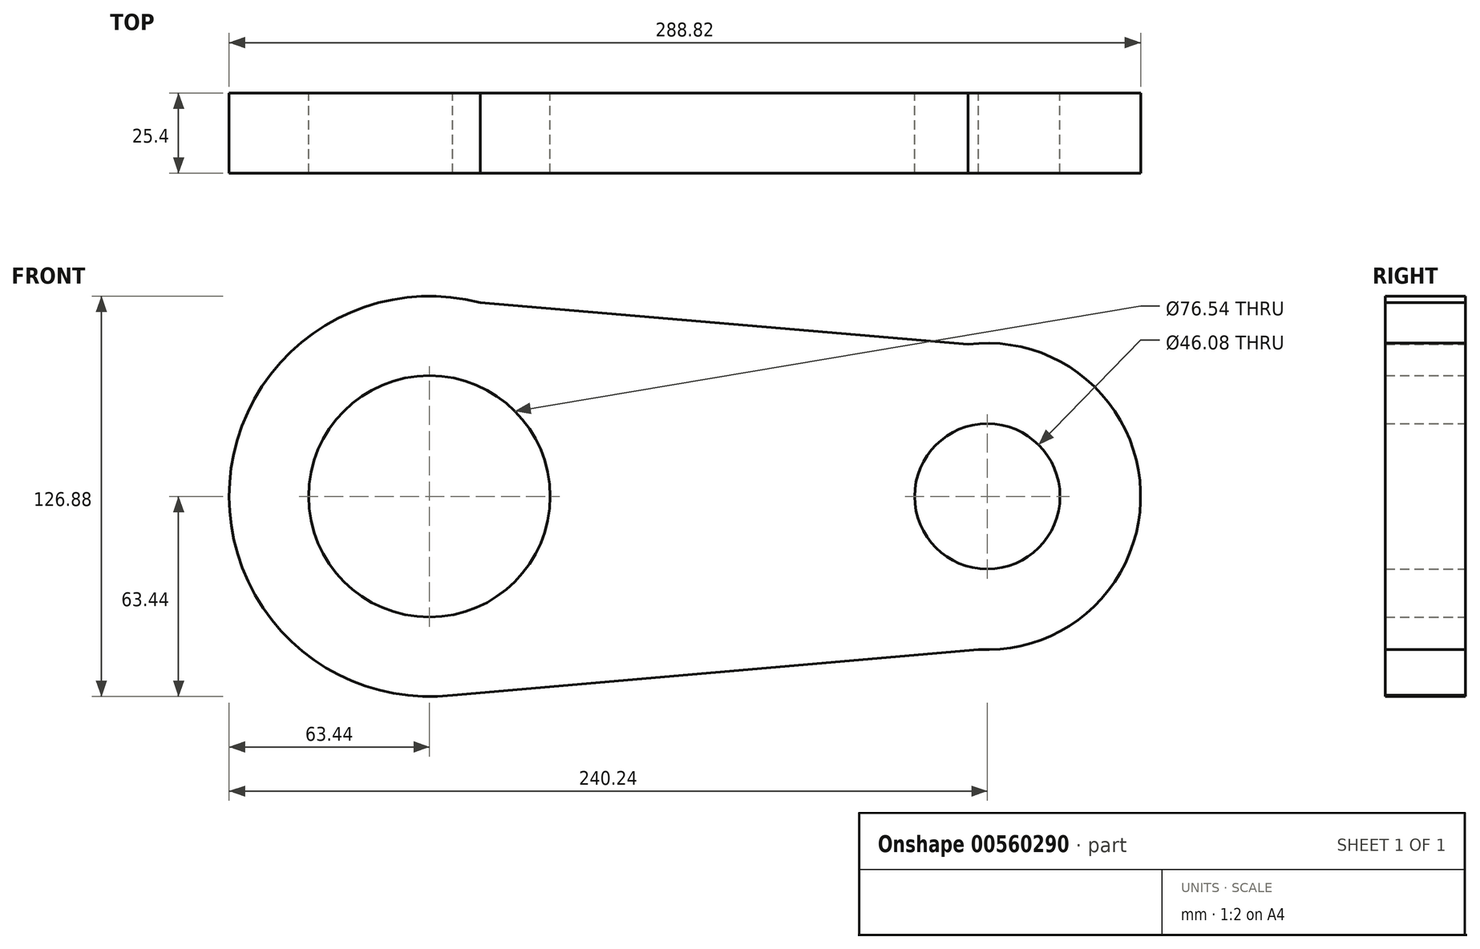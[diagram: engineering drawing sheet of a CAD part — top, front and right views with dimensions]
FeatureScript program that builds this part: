
annotation { "Feature Type Name" : "Feature", "Feature Type Description" : "" }
export const myFeature = defineFeature(function(context is Context, id is Id, definition is map)
    precondition{}
    {
        {
            var Q0;
            Q0=qCreatedBy(makeId("Front.planeOp"),FACE);
            var sketch = newSketch(context, id + "F0", { "sketchPlane" : qUnion([Q0])});
            skCircle(sketch, "E0", {"center": v(0, 0) * mm, "radius": 63.44 * mm});
            skCircle(sketch, "E1", {"center": v(176.8, 0) * mm, "radius": 48.58 * mm});
            skLineSegment(sketch, "E2", {"start": v(16.1, 61.37) * mm, "end": v(191, 46.46) * mm});
            skLineSegment(sketch, "E3", {"start": v(7.32, -63.02) * mm, "end": v(187.95, -47.28) * mm});
            skCircle(sketch, "E4", {"center": v(0, 0) * mm, "radius": 4.6 * mm});
            skCircle(sketch, "E5", {"center": v(0, 0) * mm, "radius": 38.27 * mm});
            skCircle(sketch, "E6", {"center": v(176.8, 0) * mm, "radius": 23.04 * mm});
            skSolve(sketch);
        }
        {
            var Q0;
            Q0 = qSketchRegion(id + "F0", true);
            extrude(context, id + "F1", {"entities" : qUnion([Q0]), "depth" : 25.4 * mm, "offsetDistance" : 25.4 * mm});
        }
    });
